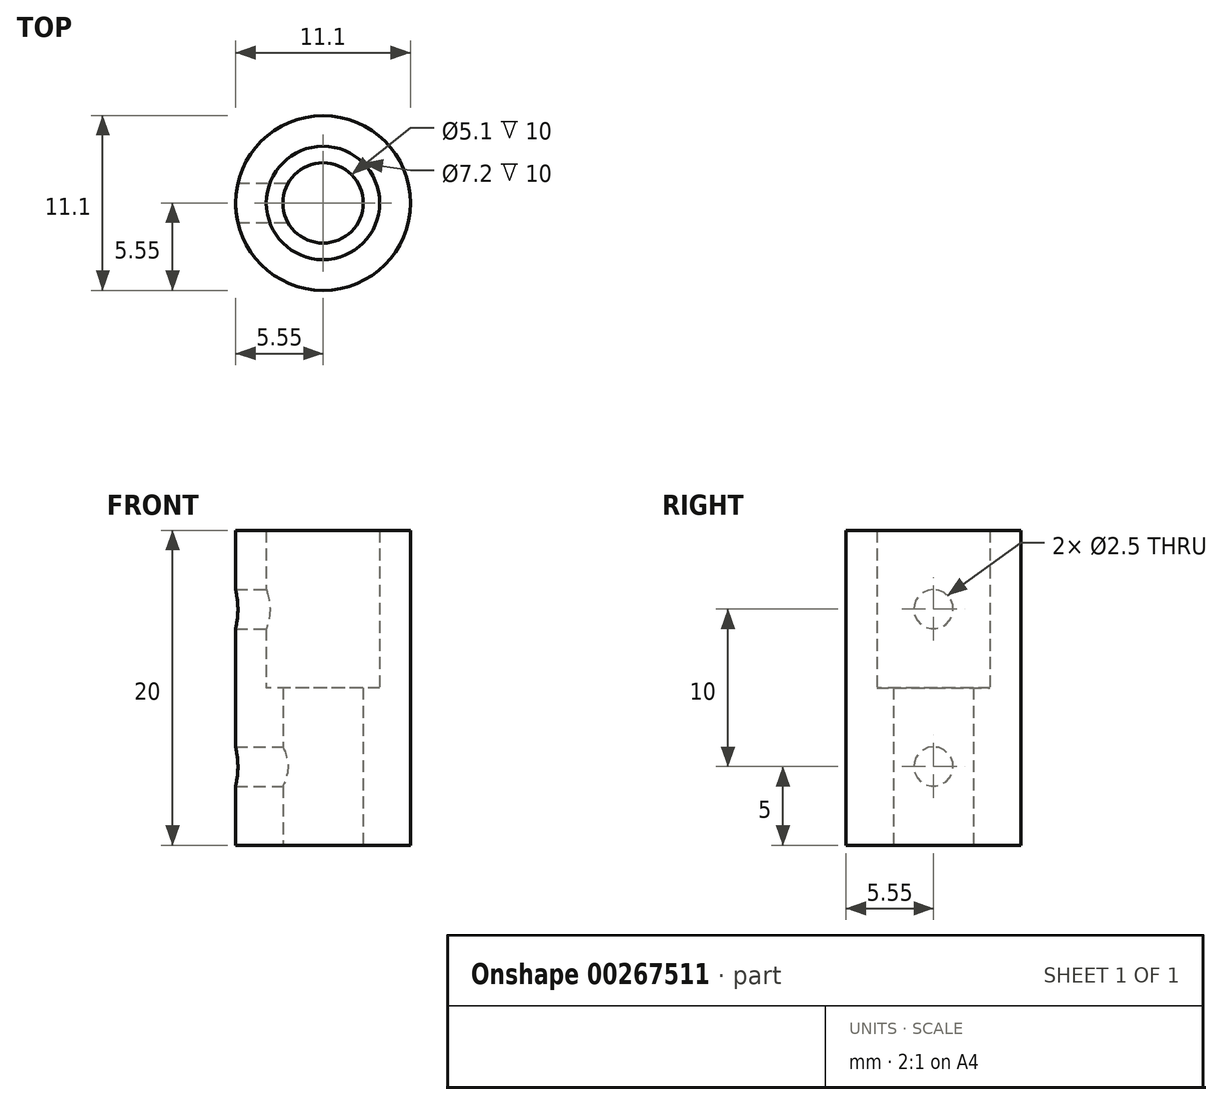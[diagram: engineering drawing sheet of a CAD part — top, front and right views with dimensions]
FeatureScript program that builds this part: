
annotation { "Feature Type Name" : "Feature", "Feature Type Description" : "" }
export const myFeature = defineFeature(function(context is Context, id is Id, definition is map)
    precondition{}
    {
        {
            var Q0;
            Q0=qCreatedBy(makeId("Top.planeOp"),FACE);
            var sketch = newSketch(context, id + "F0", { "sketchPlane" : qUnion([Q0])});
            skCircle(sketch, "E0", {"center": v(0, 0) * mm, "radius": 5.55 * mm});
            skCircle(sketch, "E1", {"center": v(0, 0) * mm, "radius": 2.55 * mm});
            skSolve(sketch);
        }
        {
            var Q0;
            Q0=makeQuery(id+"F0.imprint","IMPRINT",FACE,{"disambiguationData":[TD([[makeQuery(id+"F0.imprint","IMPRINT",EDGE,{"derivedFrom":sQuery(id+"F0.wireOp",EDGE,"E0")}),1.0]])]});
            extrude(context, id + "F1", {"entities" : qUnion([Q0]), "depth" : 10 * mm});
        }
        {
            var Q0;
            Q0=makeQuery(id+"F1.opExtrude","CAP_FACE",FACE,{"disambiguationData":[OSD([sQuery(id+"F0.wireOp",EDGE,"E0"),sQuery(id+"F0.wireOp",EDGE,"E1")])],"isStart":false});
            var sketch = newSketch(context, id + "F2", { "sketchPlane" : qUnion([Q0])});
            skCircle(sketch, "E2", {"center": v(0, 0) * mm, "radius": 3.6 * mm});
            skCircle(sketch, "E3", {"center": v(0, 0) * mm, "radius": 5.55 * mm});
            skSolve(sketch);
        }
        {
            var Q0;
            Q0 = qSketchRegion(id + "F2", true);
            extrude(context, id + "F3", {"entities" : qUnion([Q0]), "operationType" : NewBodyOperationType.ADD, "depth" : 10 * mm});
        }
        {
            var Q0;
            Q0=qCreatedBy(makeId("Right.planeOp"),FACE);
            var sketch = newSketch(context, id + "F4", { "sketchPlane" : qUnion([Q0])});
            skCircle(sketch, "E4", {"center": v(0, 15) * mm, "radius": 1.25 * mm});
            skCircle(sketch, "E5", {"center": v(0, 5) * mm, "radius": 1.25 * mm});
            skLineSegment(sketch, "E6", {"start": v(0, 20) * mm, "end": v(0, 15) * mm, "construction": true});
            skLineSegment(sketch, "E7", {"start": v(0, 15) * mm, "end": v(0, 10) * mm, "construction": true});
            skLineSegment(sketch, "E8", {"start": v(0, 10) * mm, "end": v(0, 5) * mm, "construction": true});
            skLineSegment(sketch, "E9", {"start": v(0, 5) * mm, "end": v(0, 0) * mm, "construction": true});
            skSolve(sketch);
        }
        {
            var Q0;
            Q0 = qSketchRegion(id + "F4", true);
            extrude(context, id + "F5", {"entities" : qUnion([Q0]), "operationType" : NewBodyOperationType.REMOVE, "endBound" : BoundingType.THROUGH_ALL, "oppositeDirection" : true, "depth" : 25 * mm});
        }
    });
